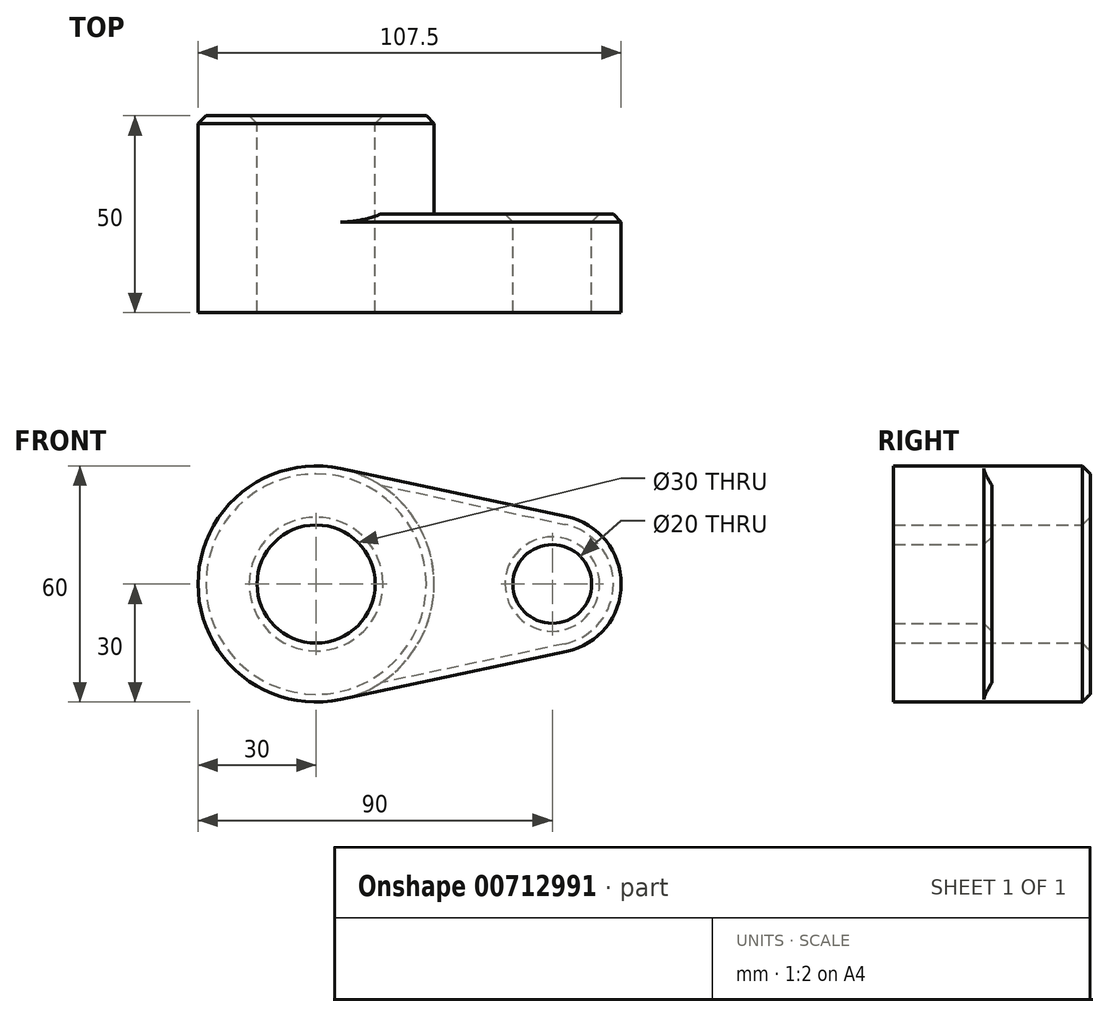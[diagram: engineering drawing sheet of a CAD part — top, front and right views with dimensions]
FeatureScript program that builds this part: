
annotation { "Feature Type Name" : "Feature", "Feature Type Description" : "" }
export const myFeature = defineFeature(function(context is Context, id is Id, definition is map)
    precondition{}
    {
        {
            var Q0;
            Q0=qCreatedBy(makeId("Front.planeOp"),FACE);
            var sketch = newSketch(context, id + "F0", { "sketchPlane" : qUnion([Q0])});
            skCircle(sketch, "E0", {"center": v(0, 0) * mm, "radius": 30 * mm});
            skCircle(sketch, "E1", {"center": v(60, 0) * mm, "radius": 17.5 * mm});
            skLineSegment(sketch, "E2", {"start": v(6.25, -29.34) * mm, "end": v(63.65, -17.12) * mm});
            skLineSegment(sketch, "E3", {"start": v(6.25, 29.34) * mm, "end": v(63.65, 17.12) * mm});
            skCircle(sketch, "E4", {"center": v(0, 0) * mm, "radius": 15 * mm});
            skCircle(sketch, "E5", {"center": v(60, 0) * mm, "radius": 10 * mm});
            skSolve(sketch);
        }
        {
            var Q0;
            Q0 = qSketchRegion(id + "F0", true);
            extrude(context, id + "F1", {"entities" : qUnion([Q0]), "depth" : 25 * mm, "offsetDistance" : 25 * mm});
        }
        {
            var Q0;
            Q0=makeQuery(id+"F0.imprint","IMPRINT",FACE,{"disambiguationData":[TD([[makeQuery(id+"F0.imprint","IMPRINT",EDGE,{"derivedFrom":sQuery(id+"F0.wireOp",EDGE,"E5")}),-1.0]])]});
            extrude(context, id + "F2", {"entities" : qUnion([Q0]), "operationType" : NewBodyOperationType.ADD, "depth" : 25 * mm, "offsetDistance" : 25 * mm});
        }
        {
            var Q0;
            Q0 = qSketchRegion(id + "F0", true);
            extrude(context, id + "F3", {"entities" : qUnion([Q0]), "operationType" : NewBodyOperationType.ADD, "depth" : 25 * mm, "offsetDistance" : 25 * mm});
        }
        {
            var Q0;
            Q0 = qSketchRegion(id + "F0", true);
            var Q1;
            Q1=makeQuery(id+"F1.opExtrude","CAP_FACE",FACE,{"disambiguationData":[OSD([sQuery(id+"F0.wireOp",EDGE,"E0"),sQuery(id+"F0.wireOp",EDGE,"E1"),sQuery(id+"F0.wireOp",EDGE,"E2"),sQuery(id+"F0.wireOp",EDGE,"E3"),sQuery(id+"F0.wireOp",EDGE,"E4"),sQuery(id+"F0.wireOp",EDGE,"E5")])],"isStart":true});
            extrude(context, id + "F4", {"entities" : qUnion([Q0, Q1]), "operationType" : NewBodyOperationType.ADD, "depth" : 25 * mm, "offsetDistance" : 25 * mm});
        }
        {
            var Q0;
            Q0=makeQuery(id+"F0.imprint","IMPRINT",FACE,{"disambiguationData":[TD([[makeQuery(id+"F0.imprint","IMPRINT",EDGE,{"derivedFrom":sQuery(id+"F0.wireOp",EDGE,"E4")}),-1.0]])]});
            extrude(context, id + "F5", {"entities" : qUnion([Q0]), "operationType" : NewBodyOperationType.ADD, "oppositeDirection" : true, "depth" : 25 * mm, "offsetDistance" : 25 * mm});
        }
        {
            var Q0;
            Q0=makeQuery(id+"F5.opExtrude","CAP_EDGE",EDGE,{"disambiguationData":[OSD([sQuery(id+"F0.wireOp",EDGE,"E4")])],"isStart":false});
            var Q1;
            Q1=makeQuery(id+"F5.opExtrude","CAP_EDGE",EDGE,{"disambiguationData":[OSD([sQuery(id+"F0.wireOp",EDGE,"E0")])],"isStart":false});
            chamfer(context, id + "F6", {"entities" : qUnion([Q0, Q1]), "width" : 2 * mm, "tangentPropagation" : true});
        }
        {
            var Q0;
            Q0=makeQuery(id+"F1.opExtrude","CAP_EDGE",EDGE,{"disambiguationData":[OSD([sQuery(id+"F0.wireOp",EDGE,"E5")])],"isStart":true});
            chamfer(context, id + "F7", {"entities" : qUnion([Q0]), "width" : 2 * mm, "tangentPropagation" : true});
        }
        {
            var Q0;
            Q0=makeQuery(id+"F1.opExtrude","CAP_EDGE",EDGE,{"disambiguationData":[OSD([sQuery(id+"F0.wireOp",EDGE,"E3")])],"isStart":true});
            var Q1;
            Q1=makeQuery(id+"F1.opExtrude","CAP_EDGE",EDGE,{"disambiguationData":[OSD([sQuery(id+"F0.wireOp",EDGE,"E2")])],"isStart":true});
            chamfer(context, id + "F8", {"entities" : qUnion([Q0, Q1]), "width" : 2 * mm, "tangentPropagation" : true});
        }
        {
            var Q0;
            Q0=qCreatedBy(makeId("Front.planeOp"),FACE);
            var sketch = newSketch(context, id + "F9", { "sketchPlane" : qUnion([Q0])});
            skCircle(sketch, "E6", {"center": v(85.26, 51) * mm, "radius": 13.46 * mm});
            skCircle(sketch, "E7", {"center": v(85.26, 51) * mm, "radius": 23.08 * mm});
            skLineSegment(sketch, "E8", {"start": v(62.26, 49.04) * mm, "end": v(42.82, 4.27) * mm});
            skLineSegment(sketch, "E9", {"start": v(99.72, 33) * mm, "end": v(72.18, -12.38) * mm});
            skSolve(sketch);
        }
        {
            var Q0;
            Q0=sQuery(id+"F9.wireOp",EDGE,"E8");
            var Q1;
            Q1=sQuery(id+"F9.wireOp",EDGE,"E9");
            var Q2;
            Q2=sQuery(id+"F9.wireOp",EDGE,"E6");
            extrude(context, id + "F10", {"bodyType" : ToolBodyType.SURFACE, "surfaceEntities" : qUnion([Q0, Q1, Q2]), "depth" : 25 * mm, "offsetDistance" : 25 * mm});
        }
    });
